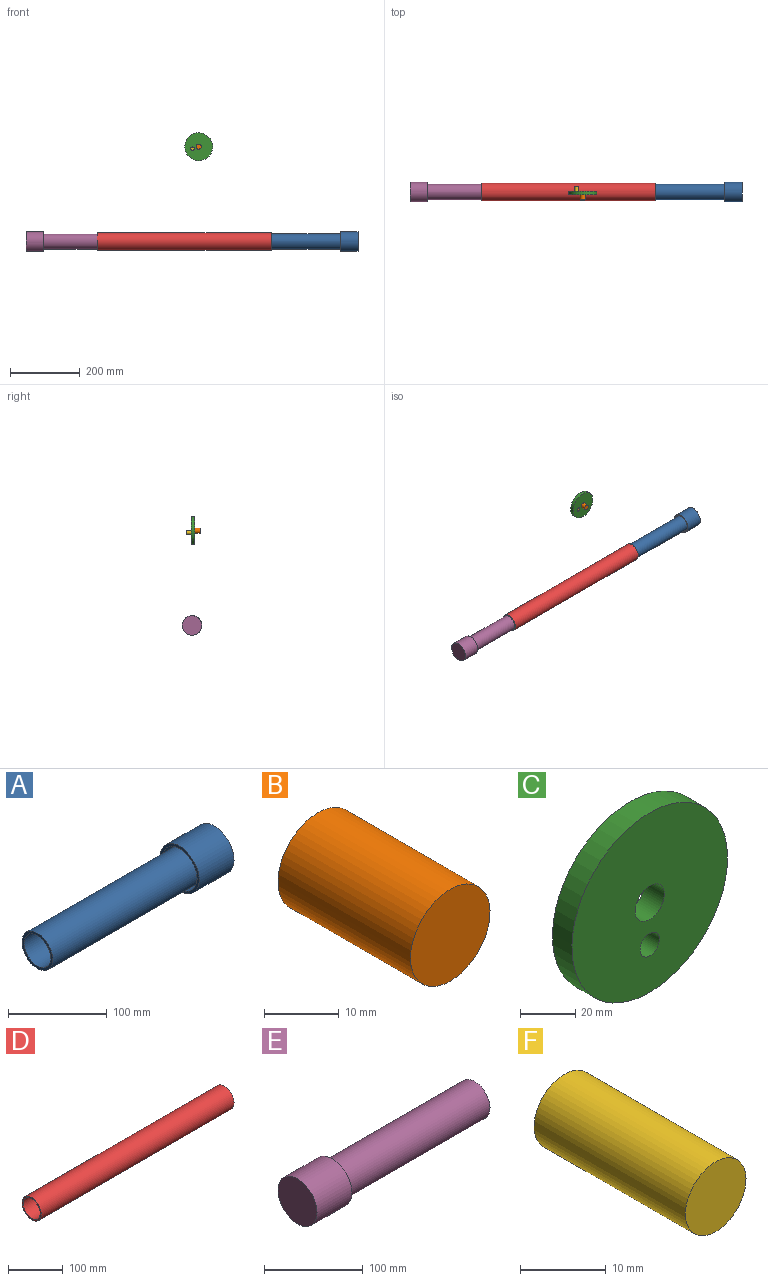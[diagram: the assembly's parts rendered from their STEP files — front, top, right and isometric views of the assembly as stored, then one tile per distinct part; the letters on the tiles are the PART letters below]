
ASSEMBLY  parts=6 mates=5
PART A: 9 faces, bbox 254.2x56x56 mm
  f0: cylinder r=25mm len=50mm, axis (-1,0,0), area 7190.4mm2, adj f1,f8
  f1: plane 50x50mm, normal (-1,0,0), area 443mm2, adj f0,f2
  f2: cylinder r=22mm len=250mm, axis (-1,0,0), area 34557.5mm2, adj f1,f3
  f3: plane 44x44mm, normal (-1,0,0), area 386.4mm2, adj f2,f4
  f4: cylinder r=19mm len=250mm, axis (-1,0,0), area 29845.1mm2, adj f3,f5
  f5: plane 38x38mm, normal (-1,0,0), area 1134.1mm2, adj f4
  f6: plane 56x56mm, normal (1,0,0), area 2463mm2, adj f7
  f7: cylinder r=28mm len=56mm, axis (-1,0,0), area 8796.5mm2, adj f6,f8
  f8: plane 56x56mm, normal (-1,0,0), area 499.5mm2, adj f0,f7
PART B: 3 faces, bbox 15x25x15 mm
  f0: cylinder r=7.5mm len=25mm, axis (0,-1,0), area 1178.1mm2, adj f1,f2
  f1: plane 15x15mm, normal (0,1,0), area 176.7mm2, adj f0
  f2: plane 15x15mm, normal (0,-1,0), area 176.7mm2, adj f0
PART C: 5 faces, bbox 80x10x80 mm
  f0: cylinder r=5mm len=10mm, axis (0,1,0), area 314.2mm2, adj f3,f4
  f1: cylinder r=7.5mm len=15mm, axis (0,1,0), area 471.2mm2, adj f3,f4
  f2: cylinder r=40mm len=80mm, axis (0,1,0), area 2513.3mm2, adj f3,f4
  f3: plane 80x80mm, normal (0,-1,0), area 4771.3mm2, adj f0,f1,f2
  f4: plane 80x80mm, normal (0,1,0), area 4771.3mm2, adj f0,f1,f2
PART D: 4 faces, bbox 500x50x50 mm
  f0: plane 50x50mm, normal (1,0,0), area 443mm2, adj f1,f3
  f1: cylinder r=25mm len=500mm, axis (1,0,0), area 78539.8mm2, adj f0,f2
  f2: plane 50x50mm, normal (-1,0,0), area 443mm2, adj f1,f3
  f3: cylinder r=22mm len=500mm, axis (1,0,0), area 69115mm2, adj f0,f2
PART E: 9 faces, bbox 254.2x56x56 mm
  f0: cylinder r=25mm len=50mm, axis (1,0,0), area 7190.4mm2, adj f1,f8
  f1: plane 56x56mm, normal (1,0,0), area 499.5mm2, adj f0,f2
  f2: cylinder r=28mm len=56mm, axis (1,0,0), area 8796.5mm2, adj f1,f3
  f3: plane 56x56mm, normal (-1,0,0), area 2463mm2, adj f2
  f4: plane 38x38mm, normal (1,0,0), area 1134.1mm2, adj f5
  f5: cylinder r=19mm len=250mm, axis (1,0,0), area 29845.1mm2, adj f4,f6
  f6: plane 44x44mm, normal (1,0,0), area 386.4mm2, adj f5,f7
  f7: cylinder r=22mm len=250mm, axis (1,0,0), area 34557.5mm2, adj f6,f8
  f8: plane 50x50mm, normal (1,0,0), area 443mm2, adj f0,f7
PART F: 3 faces, bbox 10x25x10 mm
  f0: cylinder r=5mm len=25mm, axis (0,1,0), area 785.4mm2, adj f1,f2
  f1: plane 10x10mm, normal (0,-1,0), area 78.5mm2, adj f0
  f2: plane 10x10mm, normal (0,1,0), area 78.5mm2, adj f0
PLACE A rot(axis=(1,0,0),90deg) t=(198.09,3.48,-28.57)mm
PLACE B t=(-0.25,-20,112.82)mm fixed
PLACE C rot(axis=(0,1,0),72deg) t=(-128.65,0,198.28)mm
PLACE D t=(-46.91,3.48,-28.57)mm fixed
PLACE E t=(-248.16,3.48,-28.57)mm
PLACE F rot(axis=(0,1,0),162deg) t=(-63.27,20,343.4)mm
MATE revolute C.f1 <-> B.f0  axis (0,-1,0) through (-5.64,-5,243.92)mm
MATE slider D.f1 <-> E.f0  axis (1,0,0) through (-46.91,3.48,-28.57)mm
MATE revolute B.f0 <-> C.f1  axis (0,1,0) through (-5.64,5,243.92)mm
MATE fastened F.f0 <-> C.f0  axis (0,-1,0) through (-23.4,-5,238.15)mm
MATE slider D.f1 <-> A.f0  axis (1,0,0) through (203.09,3.48,-28.57)mm
